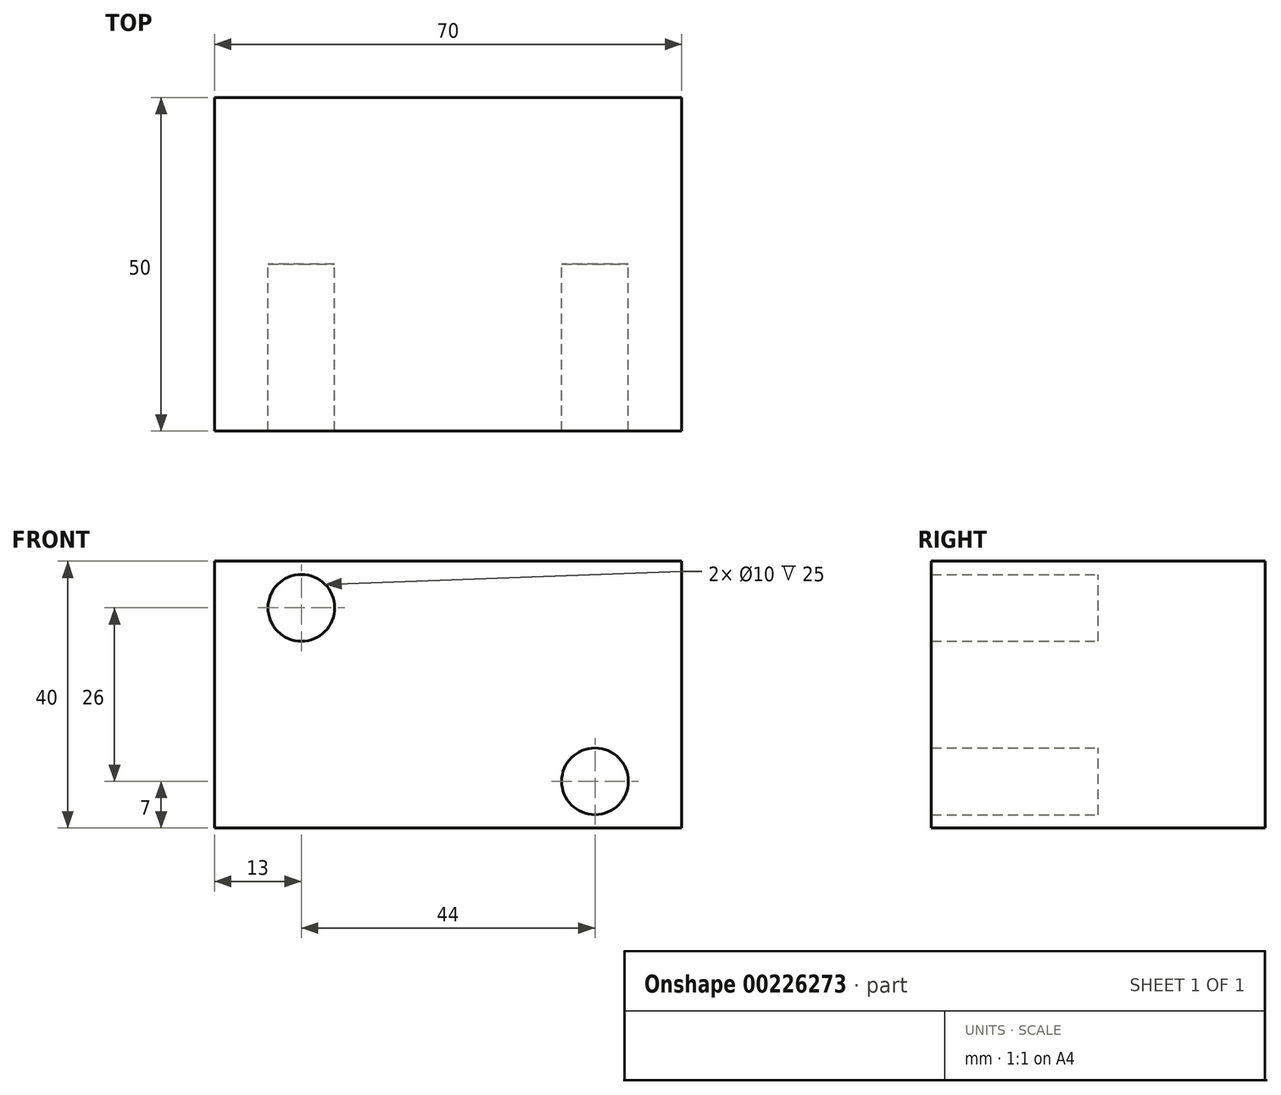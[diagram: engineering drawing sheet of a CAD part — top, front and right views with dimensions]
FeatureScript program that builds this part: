
annotation { "Feature Type Name" : "Feature", "Feature Type Description" : "" }
export const myFeature = defineFeature(function(context is Context, id is Id, definition is map)
    precondition{}
    {
        {
            var Q0;
            Q0=qCreatedBy(makeId("Front.planeOp"),FACE);
            var sketch = newSketch(context, id + "F0", { "sketchPlane" : qUnion([Q0])});
            skLineSegment(sketch, "E0.bottom", {"start": v(-35, 20) * mm, "end": v(35, 20) * mm});
            skLineSegment(sketch, "E0.top", {"start": v(-35, -20) * mm, "end": v(35, -20) * mm});
            skLineSegment(sketch, "E0.left", {"start": v(-35, 20) * mm, "end": v(-35, -20) * mm});
            skLineSegment(sketch, "E0.right", {"start": v(35, 20) * mm, "end": v(35, -20) * mm});
            skPoint(sketch, "E0.middle", {"position": v(0, 0) * mm});
            skSolve(sketch);
        }
        {
            var Q0;
            Q0=makeQuery(id+"F0.imprint","IMPRINT",FACE,{"disambiguationData":[TD([[makeQuery(id+"F0.imprint","IMPRINT",EDGE,{"derivedFrom":sQuery(id+"F0.wireOp",EDGE,"E0.bottom")}),-1.0]])]});
            extrude(context, id + "F1", {"entities" : qUnion([Q0]), "depth" : 25 * mm});
        }
        {
            var Q0;
            Q0=makeQuery(id+"F1.opExtrude","CAP_FACE",FACE,{"disambiguationData":[OSD([sQuery(id+"F0.wireOp",EDGE,"E0.bottom"),sQuery(id+"F0.wireOp",EDGE,"E0.top"),sQuery(id+"F0.wireOp",EDGE,"E0.left"),sQuery(id+"F0.wireOp",EDGE,"E0.right")])],"isStart":false});
            var sketch = newSketch(context, id + "F2", { "sketchPlane" : qUnion([Q0])});
            skCircle(sketch, "E1", {"center": v(-22, -13) * mm, "radius": 5 * mm});
            skCircle(sketch, "E2.MirrorC", {"center": v(-22, 13) * mm, "radius": 5 * mm});
            skCircle(sketch, "E3.MirrorC", {"center": v(22, 13) * mm, "radius": 5 * mm});
            skCircle(sketch, "E4.MirrorC", {"center": v(22, -13) * mm, "radius": 5 * mm});
            skSolve(sketch);
        }
        {
            var Q0;
            Q0=makeQuery(id+"F2.imprint","IMPRINT",FACE,{"disambiguationData":[TD([[makeQuery(id+"F2.imprint","IMPRINT",EDGE,{"derivedFrom":sQuery(id+"F2.wireOp",EDGE,"E1")}),1.0]])]});
            var Q1;
            Q1=makeQuery(id+"F2.imprint","IMPRINT",FACE,{"disambiguationData":[TD([[makeQuery(id+"F2.imprint","IMPRINT",EDGE,{"derivedFrom":sQuery(id+"F2.wireOp",EDGE,"E2.MirrorC")}),-1.0]])]});
            var Q2;
            Q2=makeQuery(id+"F2.imprint","IMPRINT",FACE,{"disambiguationData":[TD([[makeQuery(id+"F2.imprint","IMPRINT",EDGE,{"derivedFrom":sQuery(id+"F2.wireOp",EDGE,"E4.MirrorC")}),-1.0]])]});
            var Q3;
            Q3=makeQuery(id+"F2.imprint","IMPRINT",FACE,{"disambiguationData":[TD([[makeQuery(id+"F2.imprint","IMPRINT",EDGE,{"derivedFrom":sQuery(id+"F2.wireOp",EDGE,"E3.MirrorC")}),1.0]])]});
            extrude(context, id + "F3", {"entities" : qUnion([Q0, Q1, Q2, Q3]), "operationType" : NewBodyOperationType.ADD, "depth" : 25 * mm});
        }
    });
